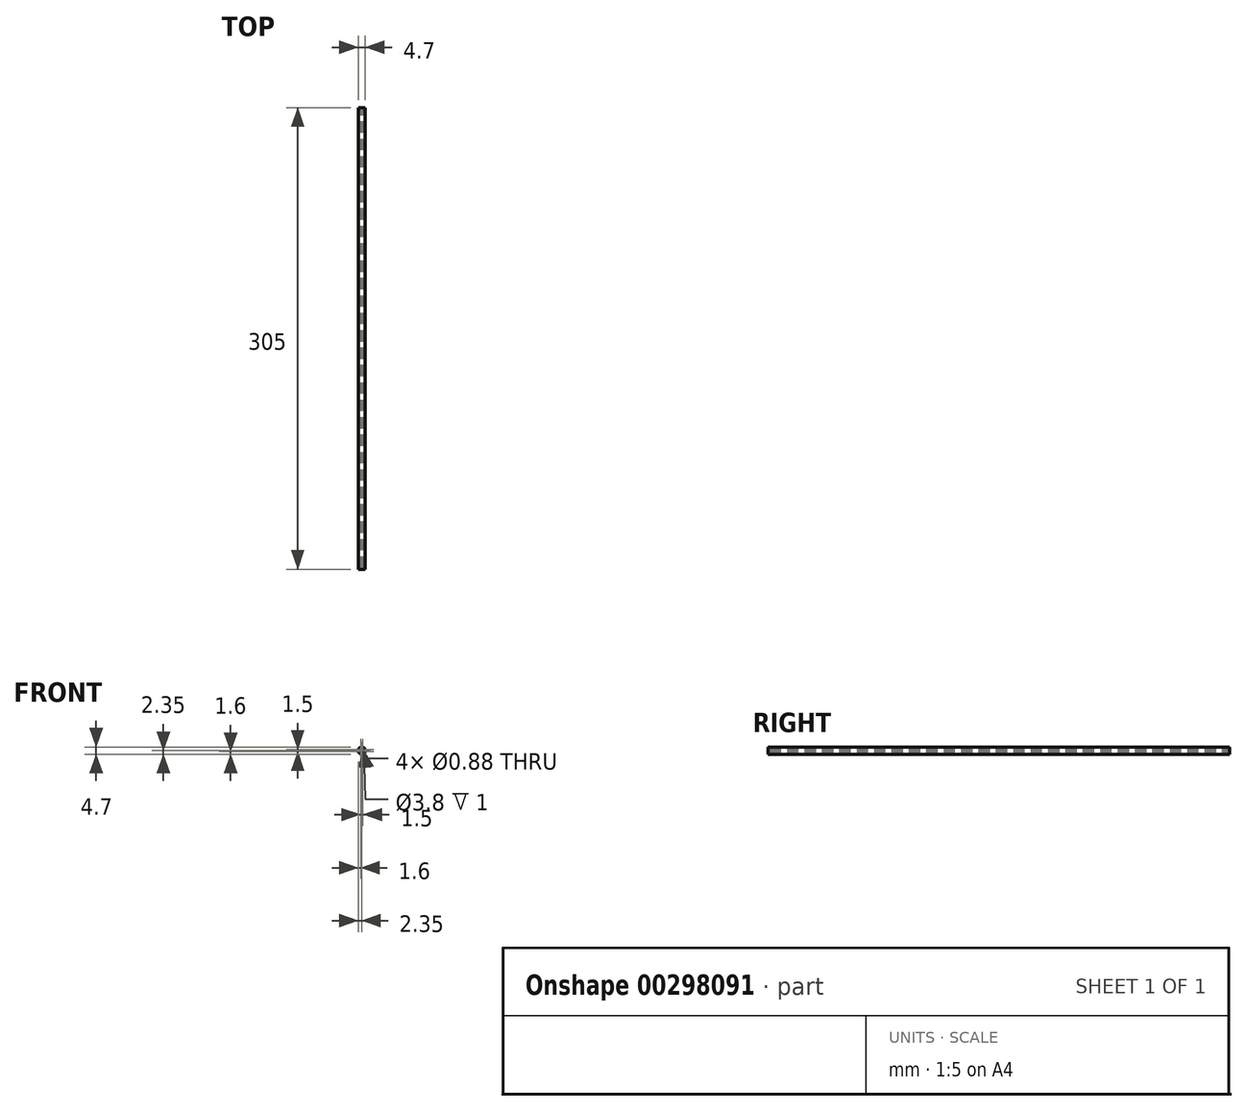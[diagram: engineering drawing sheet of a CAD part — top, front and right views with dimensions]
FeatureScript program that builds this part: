
annotation { "Feature Type Name" : "Feature", "Feature Type Description" : "" }
export const myFeature = defineFeature(function(context is Context, id is Id, definition is map)
    precondition{}
    {
        {
            var Q0;
            Q0=qCreatedBy(makeId("Front.planeOp"),FACE);
            var sketch = newSketch(context, id + "F0", { "sketchPlane" : qUnion([Q0])});
            skCircle(sketch, "E0", {"center": v(0, 0) * mm, "radius": 2.35 * mm});
            skPoint(sketch, "E1", {"position": v(0.75, 0.55) * mm});
            skCircle(sketch, "E2", {"center": v(0.75, 0.55) * mm, "radius": 0.2 * mm});
            skCircle(sketch, "E3", {"center": v(0.75, 0.95) * mm, "radius": 0.2 * mm});
            skCircle(sketch, "E4", {"center": v(0.75, 0.75) * mm, "radius": 0.44 * mm});
            skCircle(sketch, "E5", {"center": v(0, 0) * mm, "radius": 1.9 * mm});
            skCircle(sketch, "E6.1.0", {"center": v(-0.75, 0.75) * mm, "radius": 0.44 * mm});
            skCircle(sketch, "E6.1.1", {"center": v(-0.95, 0.75) * mm, "radius": 0.2 * mm});
            skCircle(sketch, "E6.1.2", {"center": v(-0.55, 0.75) * mm, "radius": 0.2 * mm});
            skCircle(sketch, "E6.2.0", {"center": v(-0.75, -0.75) * mm, "radius": 0.44 * mm});
            skCircle(sketch, "E6.2.1", {"center": v(-0.75, -0.95) * mm, "radius": 0.2 * mm});
            skCircle(sketch, "E6.2.2", {"center": v(-0.75, -0.55) * mm, "radius": 0.2 * mm});
            skCircle(sketch, "E6.3.0", {"center": v(0.75, -0.75) * mm, "radius": 0.44 * mm});
            skCircle(sketch, "E6.3.1", {"center": v(0.95, -0.75) * mm, "radius": 0.2 * mm});
            skCircle(sketch, "E6.3.2", {"center": v(0.55, -0.75) * mm, "radius": 0.2 * mm});
            skSolve(sketch);
        }
        {
            var Q0;
            Q0=makeQuery(id+"F0.imprint","IMPRINT",FACE,{"disambiguationData":[TD([[makeQuery(id+"F0.imprint","IMPRINT",EDGE,{"derivedFrom":sQuery(id+"F0.wireOp",EDGE,"E0")}),1.0]])]});
            var Q1;
            Q1=makeQuery(id+"F0.imprint","IMPRINT",FACE,{"disambiguationData":[TD([[makeQuery(id+"F0.imprint","IMPRINT",EDGE,{"derivedFrom":sQuery(id+"F0.wireOp",EDGE,"E4")}),-1.0]])]});
            extrude(context, id + "F1", {"entities" : qUnion([Q0, Q1]), "depth" : 305 * mm});
        }
        {
            var Q0;
            Q0=makeQuery(id+"F1.opExtrude","CAP_FACE",FACE,{"disambiguationData":[OSD([sQuery(id+"F0.wireOp",EDGE,"E0"),sQuery(id+"F0.wireOp",EDGE,"E4"),sQuery(id+"F0.wireOp",EDGE,"E6.1.0"),sQuery(id+"F0.wireOp",EDGE,"E6.2.0"),sQuery(id+"F0.wireOp",EDGE,"E6.3.0")])],"isStart":false});
            var sketch = newSketch(context, id + "F2", { "sketchPlane" : qUnion([Q0])});
            skCircle(sketch, "E7", {"center": v(0, 0) * mm, "radius": 1.9 * mm});
            skSolve(sketch);
        }
        {
            var Q0;
            Q0=makeQuery(id+"F2.imprint","IMPRINT",FACE,{"disambiguationData":[TD([[makeQuery(id+"F2.imprint","IMPRINT",EDGE,{"derivedFrom":sQuery(id+"F2.wireOp",EDGE,"E7")}),1.0]])]});
            extrude(context, id + "F3", {"entities" : qUnion([Q0]), "operationType" : NewBodyOperationType.REMOVE, "oppositeDirection" : true, "depth" : 1 * mm});
        }
    });
